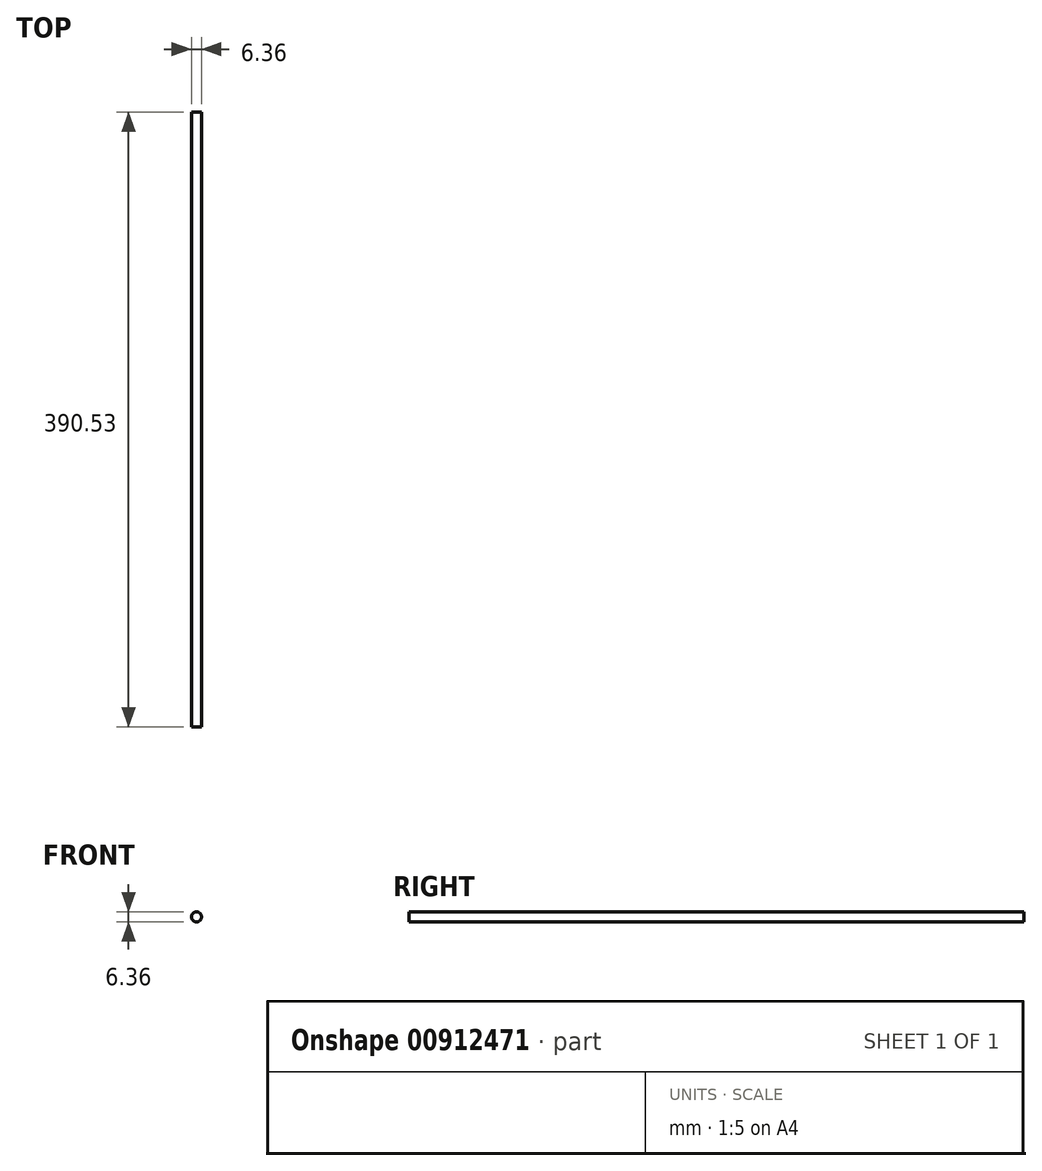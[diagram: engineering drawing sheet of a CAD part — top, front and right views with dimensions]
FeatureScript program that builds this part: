
annotation { "Feature Type Name" : "Feature", "Feature Type Description" : "" }
export const myFeature = defineFeature(function(context is Context, id is Id, definition is map)
    precondition{}
    {
        {
            var Q0;
            Q0=qCreatedBy(makeId("Front.planeOp"),FACE);
            var sketch = newSketch(context, id + "F0", { "sketchPlane" : qUnion([Q0])});
            skCircle(sketch, "E0", {"center": v(0, 0) * mm, "radius": 3.18 * mm});
            skSolve(sketch);
        }
        {
            var Q0;
            Q0 = qSketchRegion(id + "F0", true);
            extrude(context, id + "F1", {"entities" : qUnion([Q0]), "depth" : 390.52 * mm, "offsetDistance" : 25.4 * mm});
        }
    });
